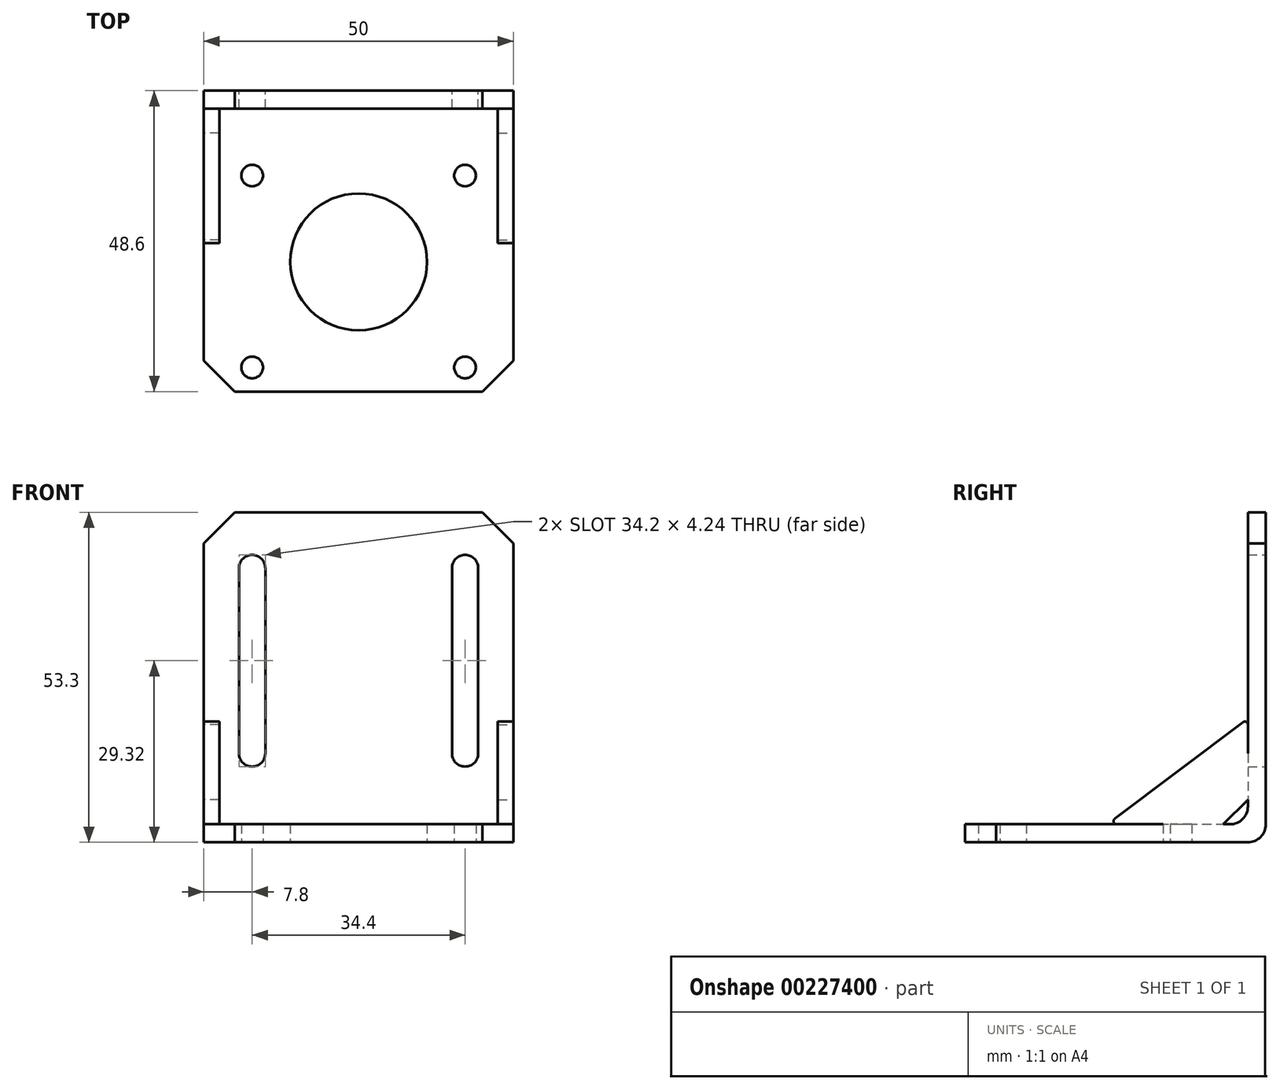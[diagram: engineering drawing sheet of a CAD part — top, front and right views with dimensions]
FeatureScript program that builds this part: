
annotation { "Feature Type Name" : "Feature", "Feature Type Description" : "" }
export const myFeature = defineFeature(function(context is Context, id is Id, definition is map)
    precondition{}
    {
        {
            var Q0;
            Q0=qCreatedBy(makeId("Front.planeOp"),FACE);
            var sketch = newSketch(context, id + "F0", { "sketchPlane" : qUnion([Q0])});
            skLineSegment(sketch, "E0.bottom", {"start": v(-25, 0) * mm, "end": v(25, 0) * mm});
            skLineSegment(sketch, "E0.top", {"start": v(-20, 53.3) * mm, "end": v(20, 53.3) * mm});
            skLineSegment(sketch, "E0.left", {"start": v(-25, 0) * mm, "end": v(-25, 48.3) * mm});
            skLineSegment(sketch, "E0.right", {"start": v(25, 0) * mm, "end": v(25, 48.3) * mm});
            skLineSegment(sketch, "E1", {"start": v(-25, 48.3) * mm, "end": v(-20, 53.3) * mm});
            skLineSegment(sketch, "E2", {"start": v(20, 53.3) * mm, "end": v(25, 48.3) * mm});
            skArc(sketch, "E3", {"start": v(19.32, 44.3) * mm, "mid": v(17.2, 46.42) * mm, "end": v(15.08, 44.3) * mm});
            skArc(sketch, "E4", {"start": v(15.08, 14.34) * mm, "mid": v(17.2, 12.22) * mm, "end": v(19.32, 14.34) * mm});
            skArc(sketch, "E5", {"start": v(-15.08, 44.3) * mm, "mid": v(-17.2, 46.42) * mm, "end": v(-19.32, 44.3) * mm});
            skArc(sketch, "E6", {"start": v(-19.32, 14.34) * mm, "mid": v(-17.2, 12.22) * mm, "end": v(-15.08, 14.34) * mm});
            skLineSegment(sketch, "E7", {"start": v(17.2, 44.3) * mm, "end": v(17.2, 14.34) * mm});
            skLineSegment(sketch, "E8", {"start": v(-17.2, 44.3) * mm, "end": v(-17.2, 14.34) * mm});
            skLineSegment(sketch, "E9", {"start": v(-19.32, 44.3) * mm, "end": v(-19.32, 14.34) * mm});
            skLineSegment(sketch, "E10", {"start": v(15.08, 44.3) * mm, "end": v(15.08, 14.34) * mm});
            skLineSegment(sketch, "E11", {"start": v(19.32, 44.3) * mm, "end": v(19.32, 14.34) * mm});
            skLineSegment(sketch, "E12", {"start": v(-15.08, 44.3) * mm, "end": v(-15.08, 14.34) * mm});
            skSolve(sketch);
        }
        {
            var Q0;
            Q0=makeQuery(id+"F0.imprint","IMPRINT",FACE,{"disambiguationData":[TD([[makeQuery(id+"F0.imprint","IMPRINT",EDGE,{"derivedFrom":sQuery(id+"F0.wireOp",EDGE,"E0.bottom")}),1.0]])]});
            extrude(context, id + "F1", {"entities" : qUnion([Q0]), "depth" : 2.9 * mm});
        }
        {
            var Q0;
            Q0=qCreatedBy(makeId("Top.planeOp"),FACE);
            var sketch = newSketch(context, id + "F2", { "sketchPlane" : qUnion([Q0])});
            skLineSegment(sketch, "E13.bottom", {"start": v(-25, 0) * mm, "end": v(25, 0) * mm});
            skLineSegment(sketch, "E13.top", {"start": v(-20, -48.6) * mm, "end": v(20, -48.6) * mm});
            skLineSegment(sketch, "E13.left", {"start": v(-25, 0) * mm, "end": v(-25, -43.6) * mm});
            skLineSegment(sketch, "E13.right", {"start": v(25, 0) * mm, "end": v(25, -43.6) * mm});
            skLineSegment(sketch, "E14", {"start": v(-20, -48.6) * mm, "end": v(-25, -43.6) * mm});
            skLineSegment(sketch, "E15", {"start": v(20, -48.6) * mm, "end": v(25, -43.6) * mm});
            skCircle(sketch, "E16", {"center": v(0, -27.65) * mm, "radius": 11.05 * mm});
            skCircle(sketch, "E17", {"center": v(17.2, -13.7) * mm, "radius": 1.75 * mm});
            skCircle(sketch, "E18", {"center": v(-17.2, -13.7) * mm, "radius": 1.75 * mm});
            skCircle(sketch, "E19", {"center": v(-17.2, -44.7) * mm, "radius": 1.75 * mm});
            skCircle(sketch, "E20", {"center": v(17.2, -44.7) * mm, "radius": 1.75 * mm});
            skSolve(sketch);
        }
        {
            var Q0;
            Q0=makeQuery(id+"F2.imprint","IMPRINT",FACE,{"disambiguationData":[TD([[makeQuery(id+"F2.imprint","IMPRINT",EDGE,{"derivedFrom":sQuery(id+"F2.wireOp",EDGE,"E13.bottom")}),-1.0]])]});
            extrude(context, id + "F3", {"entities" : qUnion([Q0]), "operationType" : NewBodyOperationType.ADD, "depth" : 2.9 * mm});
        }
        {
            var Q0;
            Q0=makeQuery(id+"F3.boolean.opBoolean","INTERSECT",EDGE,{"derivedFrom":[makeQuery(id+"F1.opExtrude","CAP_FACE",FACE,{"disambiguationData":[OSD([sQuery(id+"F0.wireOp",EDGE,"E0.bottom"),sQuery(id+"F0.wireOp",EDGE,"E0.top"),sQuery(id+"F0.wireOp",EDGE,"E0.left"),sQuery(id+"F0.wireOp",EDGE,"E0.right"),sQuery(id+"F0.wireOp",EDGE,"E1"),sQuery(id+"F0.wireOp",EDGE,"E2"),sQuery(id+"F0.wireOp",EDGE,"E3"),sQuery(id+"F0.wireOp",EDGE,"E4"),sQuery(id+"F0.wireOp",EDGE,"E5"),sQuery(id+"F0.wireOp",EDGE,"E6"),sQuery(id+"F0.wireOp",EDGE,"E9"),sQuery(id+"F0.wireOp",EDGE,"E10"),sQuery(id+"F0.wireOp",EDGE,"E11"),sQuery(id+"F0.wireOp",EDGE,"E12")])],"isStart":false}),makeQuery(id+"F3.opExtrude","CAP_FACE",FACE,{"disambiguationData":[OSD([sQuery(id+"F2.wireOp",EDGE,"E13.bottom"),sQuery(id+"F2.wireOp",EDGE,"E13.top"),sQuery(id+"F2.wireOp",EDGE,"E13.left"),sQuery(id+"F2.wireOp",EDGE,"E13.right"),sQuery(id+"F2.wireOp",EDGE,"E14"),sQuery(id+"F2.wireOp",EDGE,"E15"),sQuery(id+"F2.wireOp",EDGE,"E16"),sQuery(id+"F2.wireOp",EDGE,"E17"),sQuery(id+"F2.wireOp",EDGE,"E18"),sQuery(id+"F2.wireOp",EDGE,"E19"),sQuery(id+"F2.wireOp",EDGE,"E20")])],"isStart":false})]});
            var Q1;
            Q1=makeQuery(id+"F1.opExtrude","CAP_EDGE",EDGE,{"disambiguationData":[OSD([sQuery(id+"F0.wireOp",EDGE,"E0.bottom")])],"isStart":true});
            fillet(context, id + "F4", {"entities" : qUnion([Q0, Q1]), "radius" : 2.9 * mm, "tangentPropagation" : true, "allowEdgeOverflow" : false});
        }
        {
            var Q0;
            Q0=qCreatedBy(makeId("Right.planeOp"),FACE);
            cPlane(context, id + "F5", {"entities" : qUnion([Q0]), "cplaneType" : CPlaneType.OFFSET, "offset" : 25 * mm, "width" : 150 * mm, "height" : 150 * mm});
        }
        {
            var Q0;
            Q0=qCreatedBy(id+"F5.planeOp",FACE);
            var sketch = newSketch(context, id + "F6", { "sketchPlane" : qUnion([Q0])});
            skLineSegment(sketch, "E21", {"start": v(-24.4, 3.8) * mm, "end": v(-3.7, 19.4) * mm});
            skLineSegment(sketch, "E22", {"start": v(-6.86, 2.9) * mm, "end": v(-2.9, 6.86) * mm});
            skLineSegment(sketch, "E23", {"start": v(-2.9, 19) * mm, "end": v(-2.9, 6.86) * mm});
            skLineSegment(sketch, "E24", {"start": v(-24.1, 2.9) * mm, "end": v(-6.86, 2.9) * mm});
            skPoint(sketch, "E25.visualSharp", {"position": v(-2.9, 20) * mm});
            skArc(sketch, "E25.filletArc", {"start": v(-2.9, 19) * mm, "mid": v(-3.18, 19.44) * mm, "end": v(-3.7, 19.4) * mm});
            skPoint(sketch, "E26.visualSharp", {"position": v(-25.6, 2.9) * mm});
            skArc(sketch, "E26.filletArc", {"start": v(-24.4, 3.8) * mm, "mid": v(-24.58, 3.24) * mm, "end": v(-24.1, 2.9) * mm});
            skSolve(sketch);
        }
        {
            var Q0;
            Q0=makeQuery(id+"F6.imprint","IMPRINT",FACE,{"disambiguationData":[TD([[makeQuery(id+"F6.imprint","IMPRINT",EDGE,{"derivedFrom":sQuery(id+"F6.wireOp",EDGE,"E21")}),-1.0]])]});
            extrude(context, id + "F7", {"entities" : qUnion([Q0]), "operationType" : NewBodyOperationType.ADD, "oppositeDirection" : true, "depth" : 2.5 * mm});
        }
        {
            var Q0;
            Q0=makeQuery(id+"F1.opExtrude","SWEPT_BODY",BODY,{"disambiguationData":[OSD([sQuery(id+"F0.wireOp",EDGE,"E0.bottom"),sQuery(id+"F0.wireOp",EDGE,"E0.top"),sQuery(id+"F0.wireOp",EDGE,"E0.left"),sQuery(id+"F0.wireOp",EDGE,"E0.right"),sQuery(id+"F0.wireOp",EDGE,"E1"),sQuery(id+"F0.wireOp",EDGE,"E2"),sQuery(id+"F0.wireOp",EDGE,"E3"),sQuery(id+"F0.wireOp",EDGE,"E4"),sQuery(id+"F0.wireOp",EDGE,"E5"),sQuery(id+"F0.wireOp",EDGE,"E6"),sQuery(id+"F0.wireOp",EDGE,"E9"),sQuery(id+"F0.wireOp",EDGE,"E10"),sQuery(id+"F0.wireOp",EDGE,"E11"),sQuery(id+"F0.wireOp",EDGE,"E12")])]});
            var Q1;
            Q1=qCreatedBy(makeId("Right.planeOp"),FACE);
            mirror(context, id + "F8", {"operationType" : NewBodyOperationType.ADD, "entities" : qUnion([Q0]), "mirrorPlane" : qUnion([Q1])});
        }
    });
